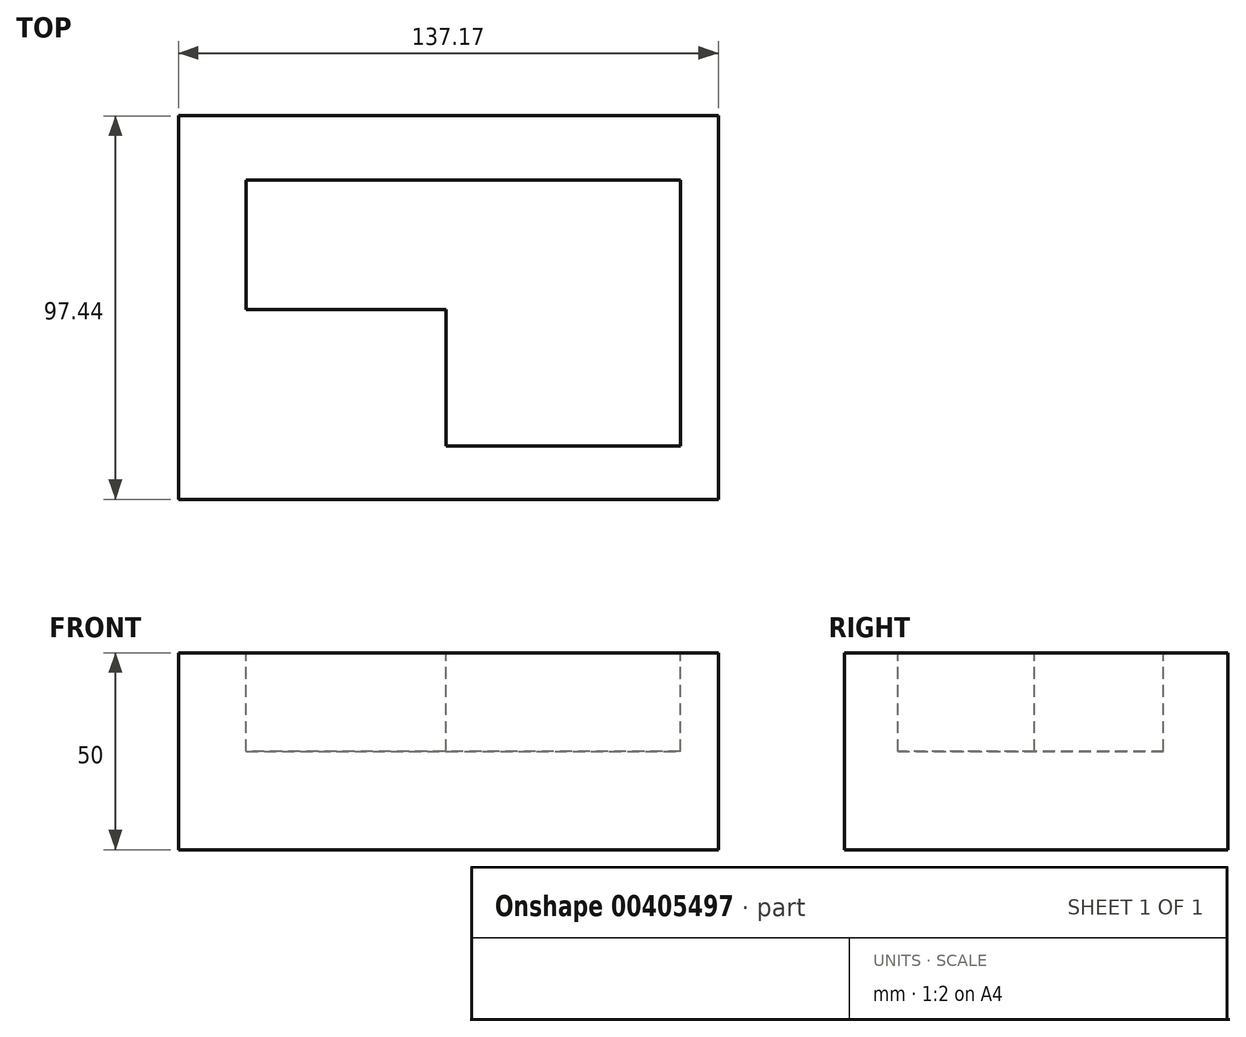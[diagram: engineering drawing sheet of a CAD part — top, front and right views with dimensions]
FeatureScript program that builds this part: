
annotation { "Feature Type Name" : "Feature", "Feature Type Description" : "" }
export const myFeature = defineFeature(function(context is Context, id is Id, definition is map)
    precondition{}
    {
        {
            var Q0;
            Q0=qCreatedBy(makeId("Top.planeOp"),FACE);
            var sketch = newSketch(context, id + "F0", { "sketchPlane" : qUnion([Q0])});
            skLineSegment(sketch, "E0.bottom", {"start": v(-68.04, 49.17) * mm, "end": v(69.13, 49.17) * mm});
            skLineSegment(sketch, "E0.top", {"start": v(-68.04, -48.27) * mm, "end": v(69.13, -48.27) * mm});
            skLineSegment(sketch, "E0.left", {"start": v(-68.04, 49.17) * mm, "end": v(-68.04, -48.27) * mm});
            skLineSegment(sketch, "E0.right", {"start": v(69.13, 49.17) * mm, "end": v(69.13, -48.27) * mm});
            skSolve(sketch);
        }
        {
            var Q0;
            Q0=makeQuery(id+"F0.imprint","IMPRINT",FACE,{"disambiguationData":[TD([[makeQuery(id+"F0.imprint","IMPRINT",EDGE,{"derivedFrom":sQuery(id+"F0.wireOp",EDGE,"E0.bottom")}),-1.0]])]});
            extrude(context, id + "F1", {"entities" : qUnion([Q0]), "depth" : 50 * mm});
        }
        {
            var Q0;
            Q0=makeQuery(id+"F1.opExtrude","CAP_FACE",FACE,{"disambiguationData":[OSD([sQuery(id+"F0.wireOp",EDGE,"E0.bottom"),sQuery(id+"F0.wireOp",EDGE,"E0.top"),sQuery(id+"F0.wireOp",EDGE,"E0.left"),sQuery(id+"F0.wireOp",EDGE,"E0.right")])],"isStart":false});
            var sketch = newSketch(context, id + "F2", { "sketchPlane" : qUnion([Q0])});
            skLineSegment(sketch, "E1", {"start": v(-50.8, 32.84) * mm, "end": v(-50.8, 0) * mm});
            skLineSegment(sketch, "E2", {"start": v(-50.8, 0) * mm, "end": v(0, 0) * mm});
            skLineSegment(sketch, "E3", {"start": v(0, 0) * mm, "end": v(0, -34.66) * mm});
            skLineSegment(sketch, "E4", {"start": v(0, -34.66) * mm, "end": v(59.52, -34.66) * mm});
            skLineSegment(sketch, "E5", {"start": v(59.52, -34.66) * mm, "end": v(59.52, 32.84) * mm});
            skLineSegment(sketch, "E6", {"start": v(59.52, 32.84) * mm, "end": v(-50.8, 32.84) * mm});
            skSolve(sketch);
        }
        {
            var Q0;
            Q0=makeQuery(id+"F2.imprint","IMPRINT",FACE,{"disambiguationData":[TD([[makeQuery(id+"F2.imprint","IMPRINT",EDGE,{"derivedFrom":sQuery(id+"F2.wireOp",EDGE,"E1")}),1.0]])]});
            extrude(context, id + "F3", {"entities" : qUnion([Q0]), "operationType" : NewBodyOperationType.REMOVE, "oppositeDirection" : true, "depth" : 25 * mm});
        }
    });
